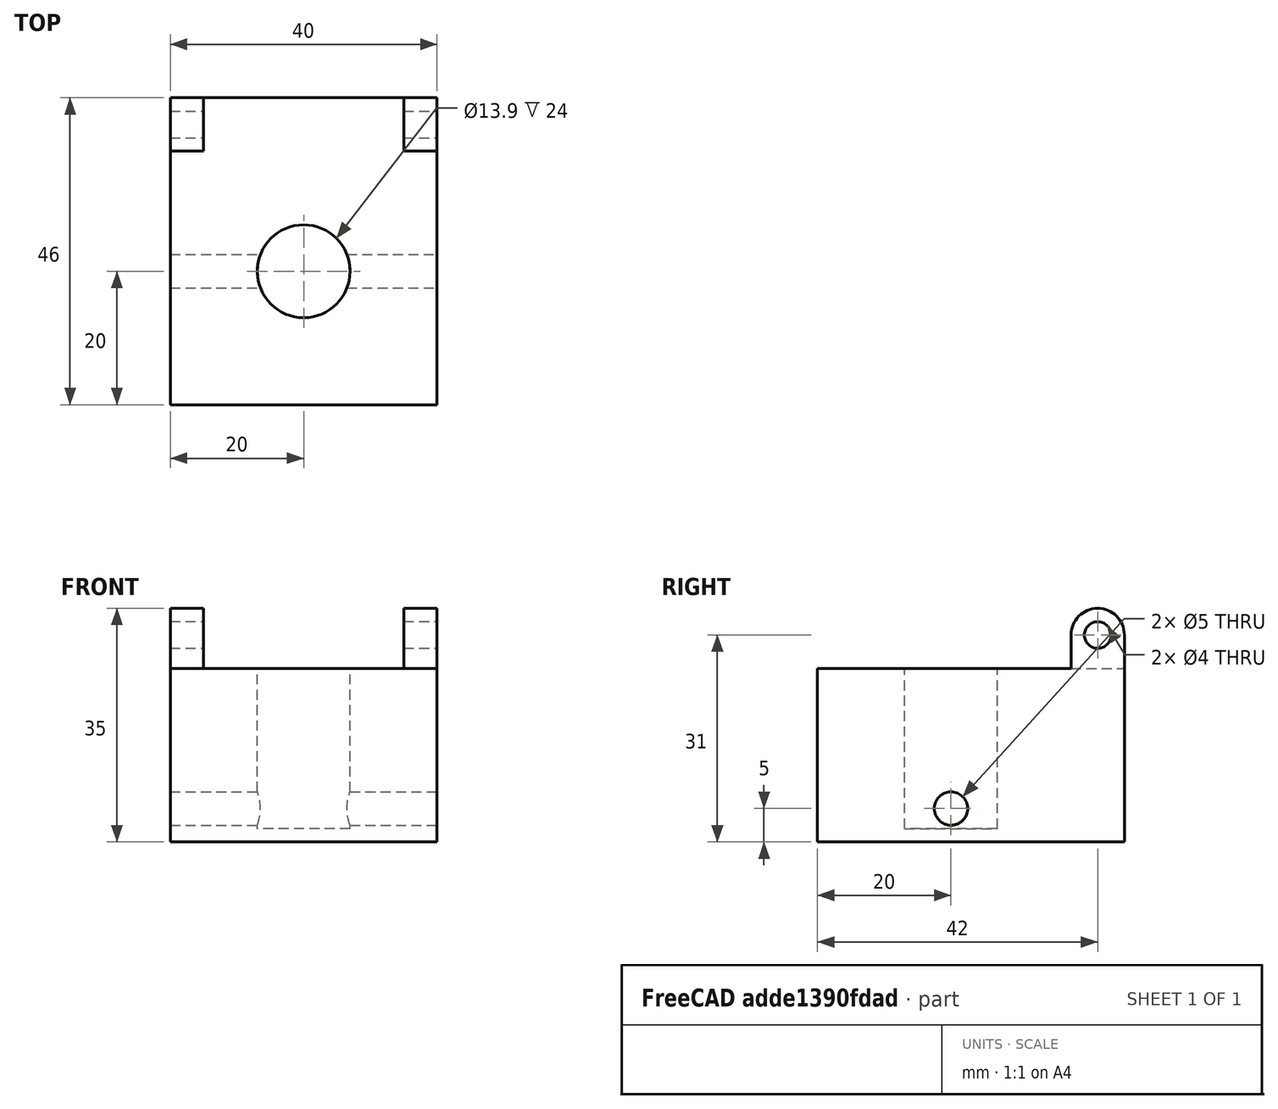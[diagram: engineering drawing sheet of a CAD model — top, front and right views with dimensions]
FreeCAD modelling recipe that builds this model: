
FCSTD DOCUMENT  (FreeCAD 0.18RUnknown)
Label: vim
License: All rights reserved
LicenseURL: http://en.wikipedia.org/wiki/All_rights_reserved
objects: Part::Cylinder×5, Part::Box×3, Part::MultiFuse×3, Part::Cut×3
note: 14 computed .brp shape members not serialized (recipe doc carries the construction recipe); baked Part::Feature solids carry a one-line shape summary decoded from their .brp

FEATURE [Part::Box] Box  label="mainbody"
  AttacherType = Attacher::AttachEngine3D
  Height = 26
  Length = 40
  Width = 46
FEATURE [Part::Cylinder] Cylinder  label="inset button"
  Angle = 360
  AttacherType = Attacher::AttachEngine3D
  Height = 24
  Placement = pos=(20,20,2) rot=(0,0,1;0rad)
  Radius = 6.95
FEATURE [Part::Cylinder] Cylinder001  label="hinge1"
  Angle = 360
  AttacherType = Attacher::AttachEngine3D
  Height = 5
  Placement = pos=(0,42,31) rot=(0,1,0;1.5708rad)
  Radius = 4
FEATURE [Part::Cylinder] Cylinder002  label="hinge2"
  Angle = 360
  AttacherType = Attacher::AttachEngine3D
  Height = 5
  Placement = pos=(35,42,31) rot=(0,1,0;1.5708rad)
  Radius = 4
FEATURE [Part::Box] Box001  label="hingeplate1"
  AttacherType = Attacher::AttachEngine3D
  Height = 5
  Length = 5
  Placement = pos=(0,38,26) rot=(0,0,1;0rad)
  Width = 8
FEATURE [Part::Box] Box002  label="hingeplate2"
  AttacherType = Attacher::AttachEngine3D
  Height = 5
  Length = 5
  Placement = pos=(35,38,26) rot=(0,0,1;0rad)
  Width = 8
FEATURE [Part::MultiFuse] Fusion  label="Hinge"
  Shapes = -> [Cylinder001,Box001]
FEATURE [Part::MultiFuse] Fusion001  label="Hinge2"
  Shapes = -> [Box002,Cylinder002]
FEATURE [Part::Cylinder] Cylinder003  label="axel"
  Angle = 360
  AttacherType = Attacher::AttachEngine3D
  Height = 45
  Placement = pos=(-2,42,31) rot=(0,1,0;1.5708rad)
  Radius = 2
FEATURE [Part::MultiFuse] Fusion002  label="buttonbody"
  Shapes = -> [Fusion001,Fusion,Box]
FEATURE [Part::Cylinder] Cylinder004  label="channel"
  Angle = 360
  AttacherType = Attacher::AttachEngine3D
  Height = 45
  Placement = pos=(-2,20,5) rot=(0,1,0;1.5708rad)
  Radius = 2.5
FEATURE [Part::Cut] Cut
  Base = -> Fusion002
  Tool = -> Cylinder004
FEATURE [Part::Cut] Cut001
  Base = -> Cut
  Tool = -> Cylinder003
FEATURE [Part::Cut] Cut002
  Base = -> Cut001
  Tool = -> Cylinder
